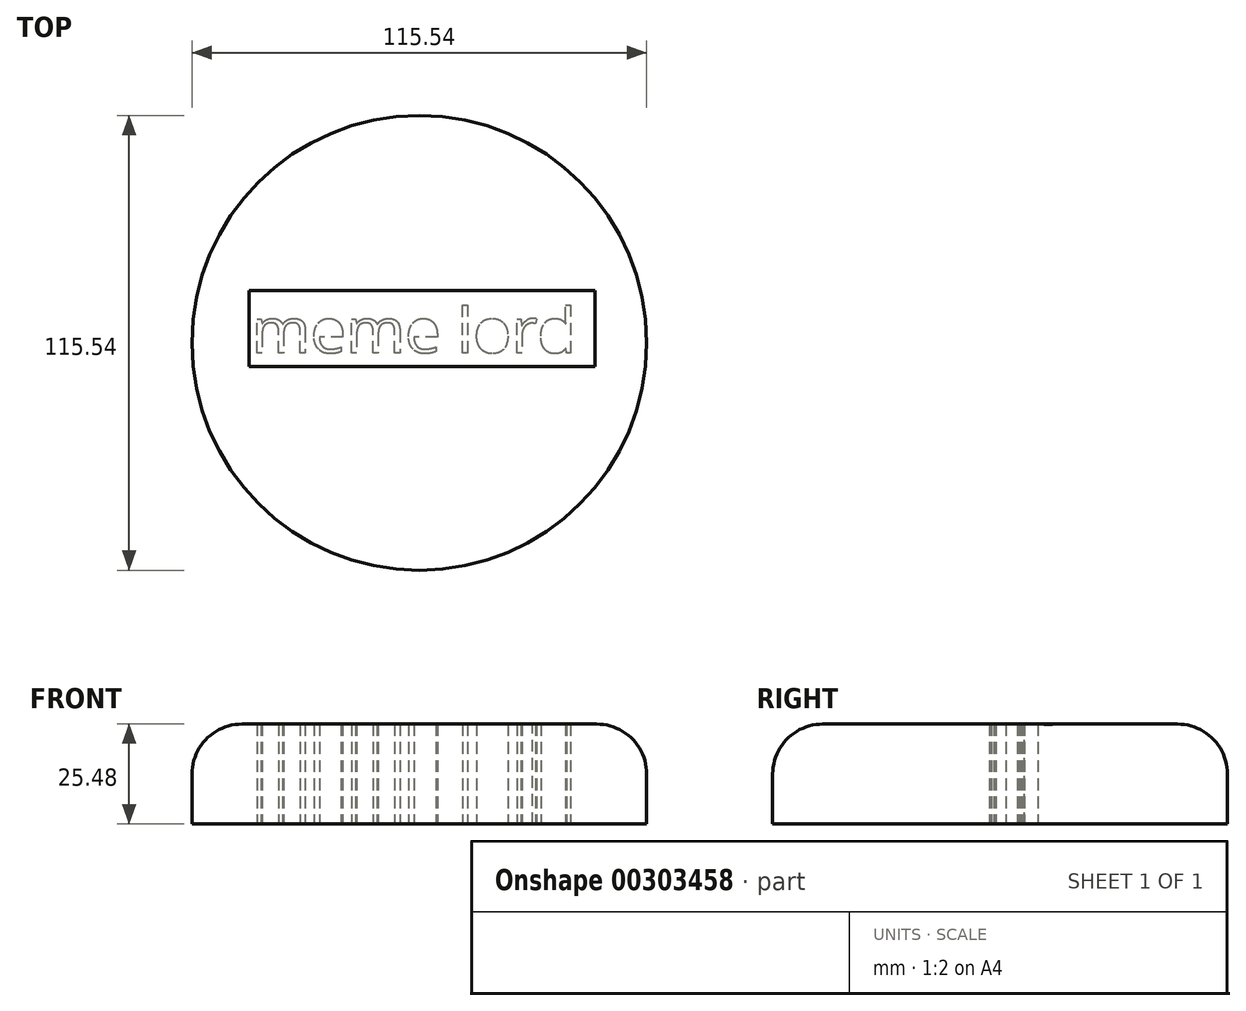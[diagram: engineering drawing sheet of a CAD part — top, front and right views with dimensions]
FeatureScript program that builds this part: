
annotation { "Feature Type Name" : "Feature", "Feature Type Description" : "" }
export const myFeature = defineFeature(function(context is Context, id is Id, definition is map)
    precondition{}
    {
        {
            var Q0;
            Q0=qCreatedBy(makeId("Top.planeOp"),FACE);
            var sketch = newSketch(context, id + "F0", { "sketchPlane" : qUnion([Q0])});
            skCircle(sketch, "E0", {"center": v(0, 0) * mm, "radius": 57.77 * mm});
            skText(sketch, "E1", { "text": "meme lord", "fontName": "OpenSans-Regular.ttf"});
            const initialGuessF0  = {"E1": [-0.04265, -0.00259, 1, 0, 0.0116]};
            skSetInitialGuess(sketch, initialGuessF0);
            skSolve(sketch);
        }
        {
            var Q0;
            Q0 = qSketchRegion(id + "F0", true);
            extrude(context, id + "F1", {"entities" : qUnion([Q0]), "depth" : 25.4 * mm});
        }
        {
            var Q0;
            Q0=makeQuery(id+"F1.opExtrude","CAP_FACE",FACE,{"disambiguationData":[OSD([sQuery(id+"F0.wireOp",EDGE,"E0"),sQuery(id+"F0.wireOp",EDGE,"E1.sketch_text.stroke-0"),sQuery(id+"F0.wireOp",EDGE,"E1.sketch_text.stroke-1"),sQuery(id+"F0.wireOp",EDGE,"E1.sketch_text.stroke-2"),sQuery(id+"F0.wireOp",EDGE,"E1.sketch_text.stroke-3"),sQuery(id+"F0.wireOp",EDGE,"E1.sketch_text.stroke-4"),sQuery(id+"F0.wireOp",EDGE,"E1.sketch_text.stroke-5"),sQuery(id+"F0.wireOp",EDGE,"E1.sketch_text.stroke-6"),sQuery(id+"F0.wireOp",EDGE,"E1.sketch_text.stroke-7"),sQuery(id+"F0.wireOp",EDGE,"E1.sketch_text.stroke-8"),sQuery(id+"F0.wireOp",EDGE,"E1.sketch_text.stroke-9"),sQuery(id+"F0.wireOp",EDGE,"E1.sketch_text.stroke-10"),sQuery(id+"F0.wireOp",EDGE,"E1.sketch_text.stroke-11"),sQuery(id+"F0.wireOp",EDGE,"E1.sketch_text.stroke-12"),sQuery(id+"F0.wireOp",EDGE,"E1.sketch_text.stroke-13"),sQuery(id+"F0.wireOp",EDGE,"E1.sketch_text.stroke-14"),sQuery(id+"F0.wireOp",EDGE,"E1.sketch_text.stroke-15"),sQuery(id+"F0.wireOp",EDGE,"E1.sketch_text.stroke-16"),sQuery(id+"F0.wireOp",EDGE,"E1.sketch_text.stroke-17"),sQuery(id+"F0.wireOp",EDGE,"E1.sketch_text.stroke-18"),sQuery(id+"F0.wireOp",EDGE,"E1.sketch_text.stroke-19"),sQuery(id+"F0.wireOp",EDGE,"E1.sketch_text.stroke-20"),sQuery(id+"F0.wireOp",EDGE,"E1.sketch_text.stroke-21"),sQuery(id+"F0.wireOp",EDGE,"E1.sketch_text.stroke-22"),sQuery(id+"F0.wireOp",EDGE,"E1.sketch_text.stroke-23"),sQuery(id+"F0.wireOp",EDGE,"E1.sketch_text.stroke-24"),sQuery(id+"F0.wireOp",EDGE,"E1.sketch_text.stroke-25"),sQuery(id+"F0.wireOp",EDGE,"E1.sketch_text.stroke-26"),sQuery(id+"F0.wireOp",EDGE,"E1.sketch_text.stroke-27"),sQuery(id+"F0.wireOp",EDGE,"E1.sketch_text.stroke-28"),sQuery(id+"F0.wireOp",EDGE,"E1.sketch_text.stroke-29"),sQuery(id+"F0.wireOp",EDGE,"E1.sketch_text.stroke-30"),sQuery(id+"F0.wireOp",EDGE,"E1.sketch_text.stroke-31"),sQuery(id+"F0.wireOp",EDGE,"E1.sketch_text.stroke-32"),sQuery(id+"F0.wireOp",EDGE,"E1.sketch_text.stroke-33"),sQuery(id+"F0.wireOp",EDGE,"E1.sketch_text.stroke-34"),sQuery(id+"F0.wireOp",EDGE,"E1.sketch_text.stroke-35"),sQuery(id+"F0.wireOp",EDGE,"E1.sketch_text.stroke-36"),sQuery(id+"F0.wireOp",EDGE,"E1.sketch_text.stroke-37"),sQuery(id+"F0.wireOp",EDGE,"E1.sketch_text.stroke-38"),sQuery(id+"F0.wireOp",EDGE,"E1.sketch_text.stroke-39"),sQuery(id+"F0.wireOp",EDGE,"E1.sketch_text.stroke-40"),sQuery(id+"F0.wireOp",EDGE,"E1.sketch_text.stroke-41"),sQuery(id+"F0.wireOp",EDGE,"E1.sketch_text.stroke-47"),sQuery(id+"F0.wireOp",EDGE,"E1.sketch_text.stroke-48"),sQuery(id+"F0.wireOp",EDGE,"E1.sketch_text.stroke-49"),sQuery(id+"F0.wireOp",EDGE,"E1.sketch_text.stroke-50"),sQuery(id+"F0.wireOp",EDGE,"E1.sketch_text.stroke-51"),sQuery(id+"F0.wireOp",EDGE,"E1.sketch_text.stroke-52"),sQuery(id+"F0.wireOp",EDGE,"E1.sketch_text.stroke-53"),sQuery(id+"F0.wireOp",EDGE,"E1.sketch_text.stroke-54"),sQuery(id+"F0.wireOp",EDGE,"E1.sketch_text.stroke-55"),sQuery(id+"F0.wireOp",EDGE,"E1.sketch_text.stroke-56"),sQuery(id+"F0.wireOp",EDGE,"E1.sketch_text.stroke-57"),sQuery(id+"F0.wireOp",EDGE,"E1.sketch_text.stroke-58"),sQuery(id+"F0.wireOp",EDGE,"E1.sketch_text.stroke-59"),sQuery(id+"F0.wireOp",EDGE,"E1.sketch_text.stroke-60"),sQuery(id+"F0.wireOp",EDGE,"E1.sketch_text.stroke-61"),sQuery(id+"F0.wireOp",EDGE,"E1.sketch_text.stroke-62"),sQuery(id+"F0.wireOp",EDGE,"E1.sketch_text.stroke-63"),sQuery(id+"F0.wireOp",EDGE,"E1.sketch_text.stroke-64"),sQuery(id+"F0.wireOp",EDGE,"E1.sketch_text.stroke-65"),sQuery(id+"F0.wireOp",EDGE,"E1.sketch_text.stroke-66"),sQuery(id+"F0.wireOp",EDGE,"E1.sketch_text.stroke-67"),sQuery(id+"F0.wireOp",EDGE,"E1.sketch_text.stroke-68"),sQuery(id+"F0.wireOp",EDGE,"E1.sketch_text.stroke-69"),sQuery(id+"F0.wireOp",EDGE,"E1.sketch_text.stroke-70"),sQuery(id+"F0.wireOp",EDGE,"E1.sketch_text.stroke-71"),sQuery(id+"F0.wireOp",EDGE,"E1.sketch_text.stroke-72"),sQuery(id+"F0.wireOp",EDGE,"E1.sketch_text.stroke-73"),sQuery(id+"F0.wireOp",EDGE,"E1.sketch_text.stroke-74"),sQuery(id+"F0.wireOp",EDGE,"E1.sketch_text.stroke-75"),sQuery(id+"F0.wireOp",EDGE,"E1.sketch_text.stroke-76"),sQuery(id+"F0.wireOp",EDGE,"E1.sketch_text.stroke-77"),sQuery(id+"F0.wireOp",EDGE,"E1.sketch_text.stroke-78"),sQuery(id+"F0.wireOp",EDGE,"E1.sketch_text.stroke-79"),sQuery(id+"F0.wireOp",EDGE,"E1.sketch_text.stroke-80"),sQuery(id+"F0.wireOp",EDGE,"E1.sketch_text.stroke-81"),sQuery(id+"F0.wireOp",EDGE,"E1.sketch_text.stroke-82"),sQuery(id+"F0.wireOp",EDGE,"E1.sketch_text.stroke-83"),sQuery(id+"F0.wireOp",EDGE,"E1.sketch_text.stroke-84"),sQuery(id+"F0.wireOp",EDGE,"E1.sketch_text.stroke-85"),sQuery(id+"F0.wireOp",EDGE,"E1.sketch_text.stroke-86"),sQuery(id+"F0.wireOp",EDGE,"E1.sketch_text.stroke-87"),sQuery(id+"F0.wireOp",EDGE,"E1.sketch_text.stroke-88"),sQuery(id+"F0.wireOp",EDGE,"E1.sketch_text.stroke-94"),sQuery(id+"F0.wireOp",EDGE,"E1.sketch_text.stroke-95"),sQuery(id+"F0.wireOp",EDGE,"E1.sketch_text.stroke-96"),sQuery(id+"F0.wireOp",EDGE,"E1.sketch_text.stroke-97"),sQuery(id+"F0.wireOp",EDGE,"E1.sketch_text.stroke-98"),sQuery(id+"F0.wireOp",EDGE,"E1.sketch_text.stroke-99"),sQuery(id+"F0.wireOp",EDGE,"E1.sketch_text.stroke-100"),sQuery(id+"F0.wireOp",EDGE,"E1.sketch_text.stroke-101"),sQuery(id+"F0.wireOp",EDGE,"E1.sketch_text.stroke-102"),sQuery(id+"F0.wireOp",EDGE,"E1.sketch_text.stroke-103"),sQuery(id+"F0.wireOp",EDGE,"E1.sketch_text.stroke-104"),sQuery(id+"F0.wireOp",EDGE,"E1.sketch_text.stroke-105"),sQuery(id+"F0.wireOp",EDGE,"E1.sketch_text.stroke-106"),sQuery(id+"F0.wireOp",EDGE,"E1.sketch_text.stroke-115"),sQuery(id+"F0.wireOp",EDGE,"E1.sketch_text.stroke-116"),sQuery(id+"F0.wireOp",EDGE,"E1.sketch_text.stroke-117"),sQuery(id+"F0.wireOp",EDGE,"E1.sketch_text.stroke-118"),sQuery(id+"F0.wireOp",EDGE,"E1.sketch_text.stroke-119"),sQuery(id+"F0.wireOp",EDGE,"E1.sketch_text.stroke-120"),sQuery(id+"F0.wireOp",EDGE,"E1.sketch_text.stroke-121"),sQuery(id+"F0.wireOp",EDGE,"E1.sketch_text.stroke-122"),sQuery(id+"F0.wireOp",EDGE,"E1.sketch_text.stroke-123"),sQuery(id+"F0.wireOp",EDGE,"E1.sketch_text.stroke-124"),sQuery(id+"F0.wireOp",EDGE,"E1.sketch_text.stroke-125"),sQuery(id+"F0.wireOp",EDGE,"E1.sketch_text.stroke-126"),sQuery(id+"F0.wireOp",EDGE,"E1.sketch_text.stroke-127"),sQuery(id+"F0.wireOp",EDGE,"E1.sketch_text.stroke-128"),sQuery(id+"F0.wireOp",EDGE,"E1.sketch_text.stroke-129"),sQuery(id+"F0.wireOp",EDGE,"E1.sketch_text.stroke-130"),sQuery(id+"F0.wireOp",EDGE,"E1.sketch_text.stroke-131"),sQuery(id+"F0.wireOp",EDGE,"E1.sketch_text.stroke-132"),sQuery(id+"F0.wireOp",EDGE,"E1.sketch_text.stroke-133"),sQuery(id+"F0.wireOp",EDGE,"E1.sketch_text.stroke-134"),sQuery(id+"F0.wireOp",EDGE,"E1.sketch_text.stroke-135"),sQuery(id+"F0.wireOp",EDGE,"E1.sketch_text.stroke-136"),sQuery(id+"F0.wireOp",EDGE,"E1.sketch_text.stroke-137"),sQuery(id+"F0.wireOp",EDGE,"E1.sketch_text.stroke-138"),sQuery(id+"F0.wireOp",EDGE,"E1.sketch_text.stroke-139"),sQuery(id+"F0.wireOp",EDGE,"E1.sketch_text.stroke-140"),sQuery(id+"F0.wireOp",EDGE,"E1.sketch_text.stroke-141"),sQuery(id+"F0.wireOp",EDGE,"E1.sketch_text.stroke-142")])],"isStart":false});
            var sketch = newSketch(context, id + "F2", { "sketchPlane" : qUnion([Q0])});
            skLineSegment(sketch, "E2.bottom", {"start": v(-43.27, -5.97) * mm, "end": v(44.57, -5.97) * mm});
            skLineSegment(sketch, "E2.top", {"start": v(-43.27, 13.24) * mm, "end": v(44.57, 13.24) * mm});
            skLineSegment(sketch, "E2.left", {"start": v(-43.27, -5.97) * mm, "end": v(-43.27, 13.24) * mm});
            skLineSegment(sketch, "E2.right", {"start": v(44.57, -5.97) * mm, "end": v(44.57, 13.24) * mm});
            skSolve(sketch);
        }
        {
            var Q0;
            Q0 = qSketchRegion(id + "F2", true);
            extrude(context, id + "F3", {"entities" : qUnion([Q0]), "operationType" : NewBodyOperationType.ADD, "depth" : 0.08 * mm});
        }
        {
            var Q0;
            Q0=makeQuery(id+"F1.opExtrude","CAP_EDGE",EDGE,{"disambiguationData":[OSD([sQuery(id+"F0.wireOp",EDGE,"E0")])],"isStart":false});
            fillet(context, id + "F4", {"entities" : qUnion([Q0]), "radius" : 12.7 * mm, "tangentPropagation" : true, "allowEdgeOverflow" : false});
        }
    });
